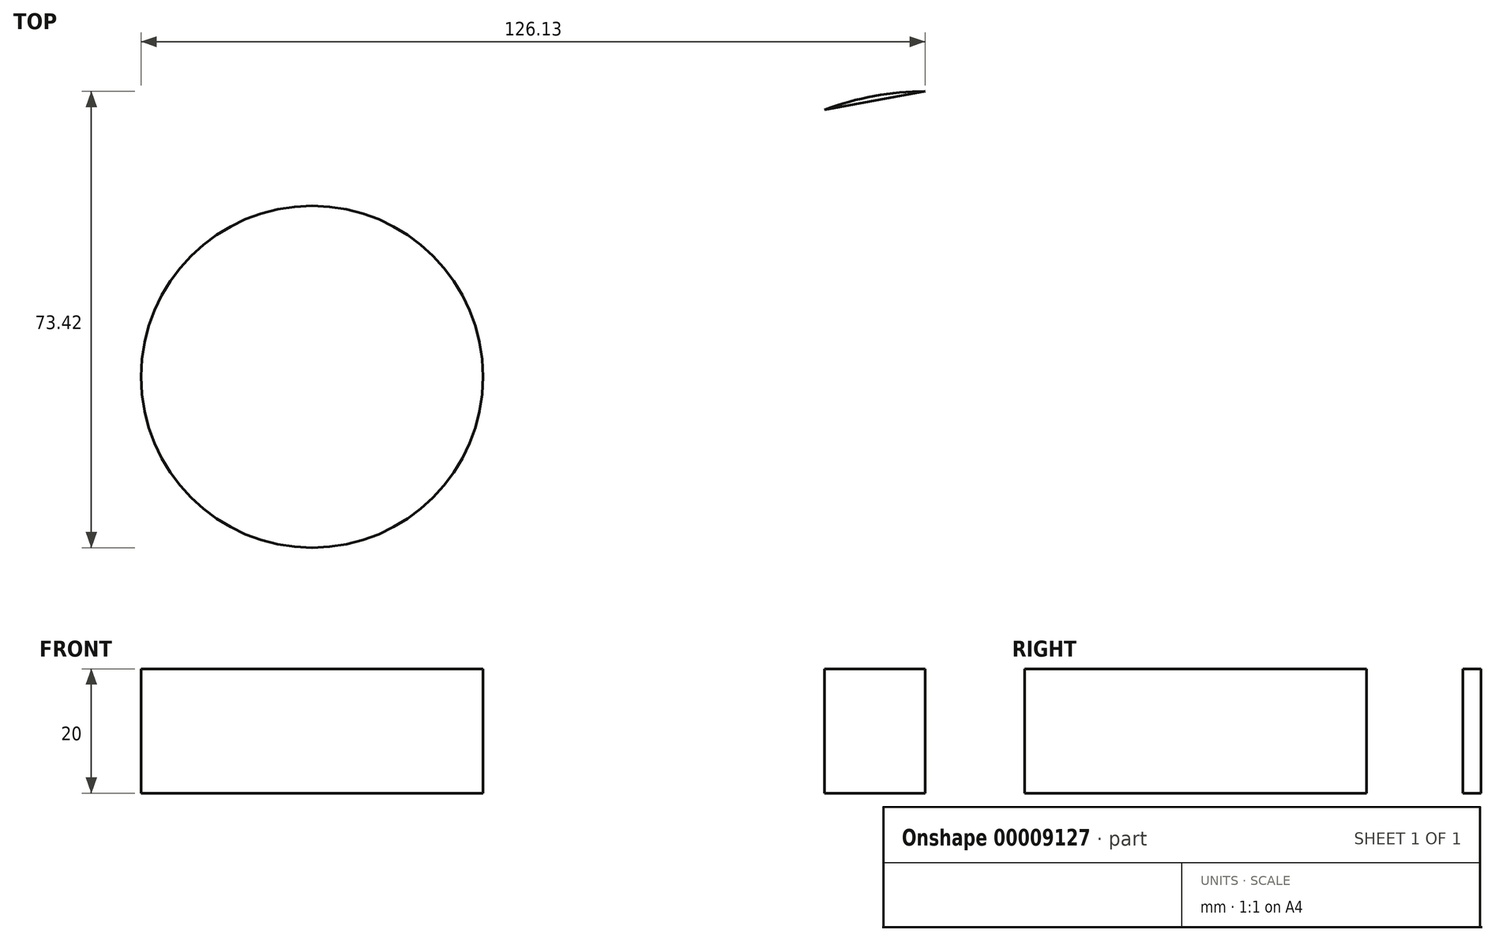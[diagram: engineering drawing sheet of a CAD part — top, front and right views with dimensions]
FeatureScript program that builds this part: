
annotation { "Feature Type Name" : "Feature", "Feature Type Description" : "" }
export const myFeature = defineFeature(function(context is Context, id is Id, definition is map)
    precondition{}
    {
        {
            var Q0;
            Q0=qCreatedBy(makeId("Top.planeOp"),FACE);
            var sketch = newSketch(context, id + "F0", { "sketchPlane" : qUnion([Q0])});
            skCircle(sketch, "E0", {"center": v(0, 0) * mm, "radius": 45.92 * mm});
            skCircle(sketch, "E1", {"center": v(-98.63, 0) * mm, "radius": 27.5 * mm});
            skLineSegment(sketch, "E2", {"start": v(-100.62, -27.43) * mm, "end": v(0, -45.92) * mm});
            skLineSegment(sketch, "E3", {"start": v(0, 45.92) * mm, "end": v(-103.56, 27.05) * mm});
            skSolve(sketch);
        }
        {
            var Q0;
            {var subQ0=sQuery(id+"F0.wireOp",EDGE,"E1");var subQ2=makeQuery(id+"F0.imprint","INTERSECT",VERTEX,{"derivedFrom":[subQ0,sQuery(id+"F0.wireOp",EDGE,"E2")]});Q0=makeQuery(id+"F0.imprint","IMPRINT",FACE,{"disambiguationData":[TD([[makeQuery(id+"F0.imprint","IMPRINT",EDGE,{"disambiguationData":[TD([[subQ2,1.0]])],"derivedFrom":subQ0}),1.0]])]});}
            var Q1;
            {var subQ0=sQuery(id+"F0.wireOp",EDGE,"E3");var subQ1=sQuery(id+"F0.wireOp",EDGE,"E0");var subQ2=makeQuery(id+"F0.imprint","INTERSECT",VERTEX,{"disambiguationData":[OD(1.0)],"derivedFrom":[subQ1,subQ0]});Q1=makeQuery(id+"F0.imprint","IMPRINT",FACE,{"disambiguationData":[TD([[makeQuery(id+"F0.imprint","IMPRINT",EDGE,{"disambiguationData":[TD([[subQ2,-1.0]])],"derivedFrom":subQ1}),-1.0]])]});}
            var Q2;
            {var subQ0=sQuery(id+"F0.wireOp",EDGE,"E3");var subQ1=sQuery(id+"F0.wireOp",EDGE,"E0");var subQ2=makeQuery(id+"F0.imprint","INTERSECT",VERTEX,{"disambiguationData":[OD(1.0)],"derivedFrom":[subQ1,subQ0]});Q2=makeQuery(id+"F0.imprint","IMPRINT",FACE,{"disambiguationData":[TD([[makeQuery(id+"F0.imprint","IMPRINT",EDGE,{"disambiguationData":[TD([[subQ2,-1.0]])],"derivedFrom":subQ1}),1.0]])]});}
            extrude(context, id + "F1", {"entities" : qUnion([Q0, Q1, Q2]), "depth" : 20 * mm});
        }
    });
